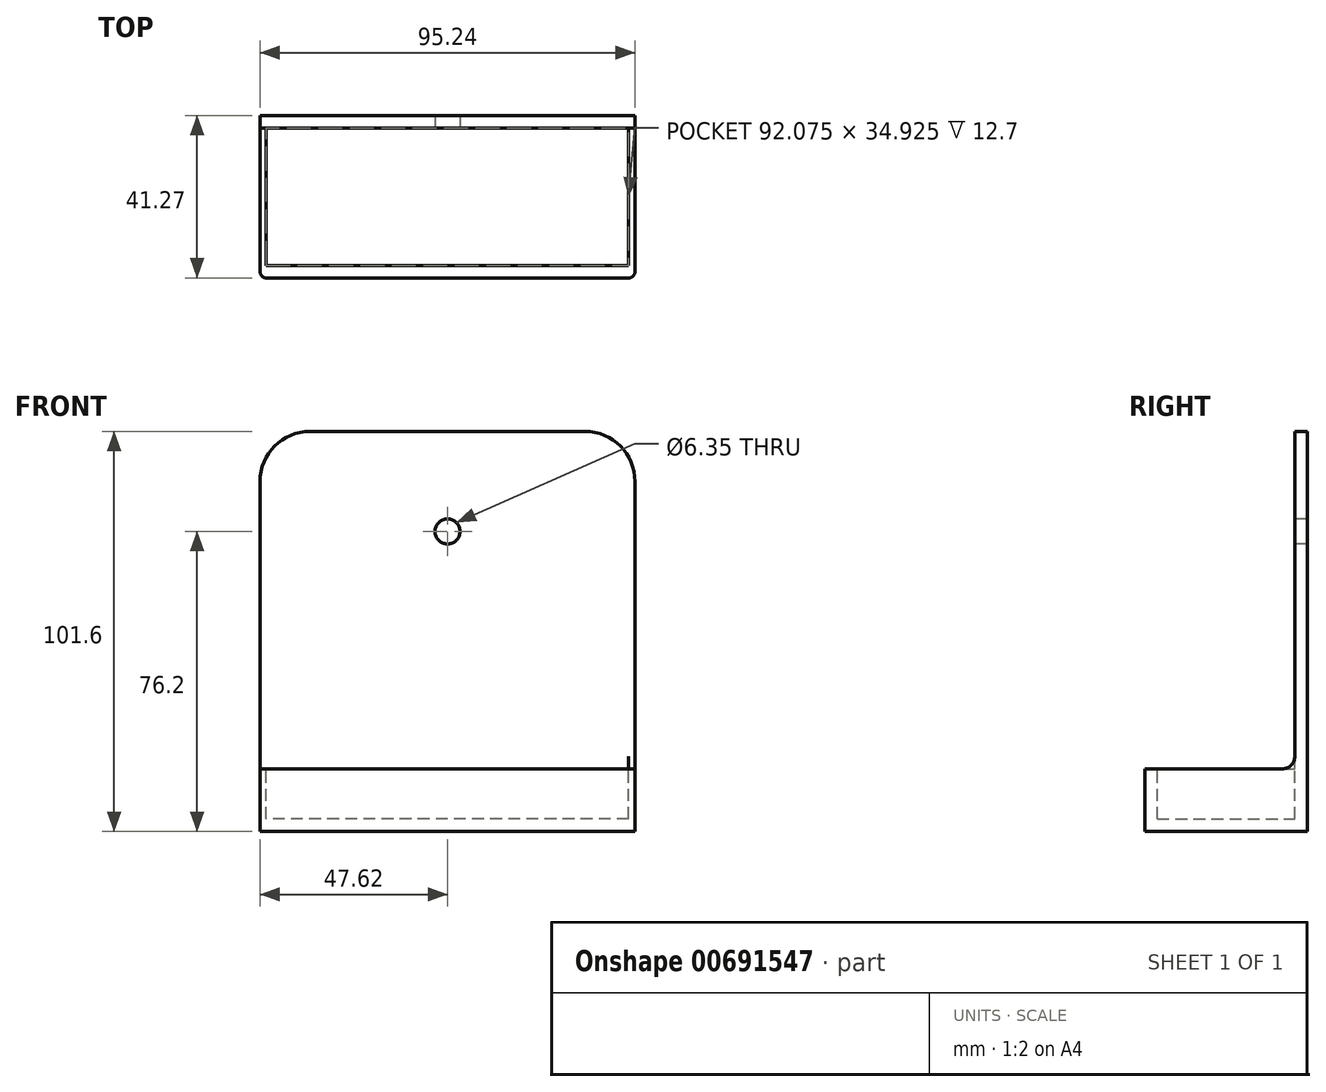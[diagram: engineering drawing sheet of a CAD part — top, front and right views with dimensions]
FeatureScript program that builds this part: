
annotation { "Feature Type Name" : "Feature", "Feature Type Description" : "" }
export const myFeature = defineFeature(function(context is Context, id is Id, definition is map)
    precondition{}
    {
        {
            var Q0;
            Q0=qCreatedBy(makeId("Front.planeOp"),FACE);
            var sketch = newSketch(context, id + "F0", { "sketchPlane" : qUnion([Q0])});
            skLineSegment(sketch, "E0", {"start": v(0, 0) * mm, "end": v(47.63, 0) * mm});
            skLineSegment(sketch, "E1", {"start": v(47.63, 0) * mm, "end": v(47.63, 101.6) * mm});
            skLineSegment(sketch, "E2", {"start": v(47.63, 101.6) * mm, "end": v(0, 101.6) * mm});
            skLineSegment(sketch, "E3", {"start": v(0, 0) * mm, "end": v(0, 39.02) * mm, "construction": true});
            skLineSegment(sketch, "E4.MirrorCS", {"start": v(-47.63, 101.6) * mm, "end": v(0, 101.6) * mm});
            skLineSegment(sketch, "E5.MirrorCS", {"start": v(-47.63, 0) * mm, "end": v(-47.63, 101.6) * mm});
            skLineSegment(sketch, "E6.MirrorCS", {"start": v(0, 0) * mm, "end": v(-47.63, 0) * mm});
            skSolve(sketch);
        }
        {
            var Q0;
            Q0=makeQuery(id+"F0.imprint","IMPRINT",FACE,{"disambiguationData":[TD([[makeQuery(id+"F0.imprint","IMPRINT",EDGE,{"derivedFrom":sQuery(id+"F0.wireOp",EDGE,"E0")}),1.0]])]});
            extrude(context, id + "F1", {"entities" : qUnion([Q0]), "depth" : 3.17 * mm, "offsetDistance" : 25.4 * mm});
        }
        {
            var Q0;
            Q0=qCreatedBy(makeId("Top.planeOp"),FACE);
            var sketch = newSketch(context, id + "F2", { "sketchPlane" : qUnion([Q0])});
            skLineSegment(sketch, "E7", {"start": v(0, 0) * mm, "end": v(-47.63, 0) * mm});
            skLineSegment(sketch, "E8", {"start": v(-47.63, 0) * mm, "end": v(-47.63, -38.1) * mm});
            skLineSegment(sketch, "E9", {"start": v(-47.63, -38.1) * mm, "end": v(0, -38.1) * mm});
            skLineSegment(sketch, "E10", {"start": v(0, 0) * mm, "end": v(0, -19.77) * mm, "construction": true});
            skLineSegment(sketch, "E11.MirrorCS", {"start": v(47.63, 0) * mm, "end": v(47.63, -38.1) * mm});
            skLineSegment(sketch, "E12.MirrorCS", {"start": v(47.63, -38.1) * mm, "end": v(0, -38.1) * mm});
            skLineSegment(sketch, "E13.MirrorCS", {"start": v(0, 0) * mm, "end": v(47.63, 0) * mm});
            skSolve(sketch);
        }
        {
            var Q0;
            Q0=makeQuery(id+"F2.imprint","IMPRINT",FACE,{"disambiguationData":[TD([[makeQuery(id+"F2.imprint","IMPRINT",EDGE,{"derivedFrom":sQuery(id+"F2.wireOp",EDGE,"E7")}),1.0]])]});
            extrude(context, id + "F3", {"entities" : qUnion([Q0]), "operationType" : NewBodyOperationType.ADD, "depth" : 3.17 * mm, "offsetDistance" : 25.4 * mm});
        }
        {
            var Q0;
            Q0=makeQuery(id+"F3.boolean.opBoolean","MERGE",FACE,{"derivedFrom":[makeQuery(id+"F1.opExtrude","SWEPT_FACE",FACE,{"disambiguationData":[OSD([sQuery(id+"F0.wireOp",EDGE,"E1")])]}),makeQuery(id+"F3.opExtrude","SWEPT_FACE",FACE,{"disambiguationData":[OSD([sQuery(id+"F2.wireOp",EDGE,"E11.MirrorCS")])]})]});
            var sketch = newSketch(context, id + "F4", { "sketchPlane" : qUnion([Q0])});
            skLineSegment(sketch, "E14", {"start": v(0, 0) * mm, "end": v(0, 15.88) * mm});
            skLineSegment(sketch, "E15", {"start": v(0, 0) * mm, "end": v(-38.1, 0) * mm});
            skLineSegment(sketch, "E16", {"start": v(-38.1, 0) * mm, "end": v(-38.1, 15.88) * mm});
            skLineSegment(sketch, "E17", {"start": v(-38.1, 15.88) * mm, "end": v(0, 15.88) * mm});
            skSolve(sketch);
        }
        {
            var Q0;
            Q0 = qSketchRegion(id + "F4", true);
            extrude(context, id + "F5", {"entities" : qUnion([Q0]), "operationType" : NewBodyOperationType.ADD, "oppositeDirection" : true, "depth" : 1.59 * mm, "offsetDistance" : 25.4 * mm});
        }
        {
            var Q0;
            Q0=makeQuery(id+"F1.opExtrude","SWEPT_BODY",BODY,{"disambiguationData":[OSD([sQuery(id+"F0.wireOp",EDGE,"E0"),sQuery(id+"F0.wireOp",EDGE,"E1"),sQuery(id+"F0.wireOp",EDGE,"E2"),sQuery(id+"F0.wireOp",EDGE,"E4.MirrorCS"),sQuery(id+"F0.wireOp",EDGE,"E5.MirrorCS"),sQuery(id+"F0.wireOp",EDGE,"E6.MirrorCS")])]});
            var Q1;
            Q1=qCreatedBy(makeId("Right.planeOp"),FACE);
            mirror(context, id + "F6", {"operationType" : NewBodyOperationType.ADD, "entities" : qUnion([Q0]), "mirrorPlane" : qUnion([Q1])});
        }
        {
            var Q0;
            {var subQ0=makeQuery(id+"F5.boolean.opBoolean","MERGE",FACE,{"derivedFrom":[makeQuery(id+"F3.opExtrude","SWEPT_FACE",FACE,{"disambiguationData":[OSD([sQuery(id+"F2.wireOp",EDGE,"E9"),sQuery(id+"F2.wireOp",EDGE,"E12.MirrorCS")])]}),makeQuery(id+"F5.opExtrude","SWEPT_FACE",FACE,{"disambiguationData":[OSD([sQuery(id+"F4.wireOp",EDGE,"E16")])]})]});Q0=makeQuery(id+"F6.boolean.opBoolean","MERGE",FACE,{"derivedFrom":[subQ0,makeQuery(id+"F6.opPattern","COPY",FACE,{"derivedFrom":subQ0,"instanceName":"1"})]});}
            var sketch = newSketch(context, id + "F7", { "sketchPlane" : qUnion([Q0])});
            skLineSegment(sketch, "E18", {"start": v(-47.63, 15.88) * mm, "end": v(47.63, 15.88) * mm});
            skLineSegment(sketch, "E19", {"start": v(47.63, 15.88) * mm, "end": v(47.63, 0) * mm});
            skLineSegment(sketch, "E20", {"start": v(47.63, 0) * mm, "end": v(-47.63, 0) * mm});
            skLineSegment(sketch, "E21", {"start": v(-47.63, 0) * mm, "end": v(-47.63, 15.88) * mm});
            skLineSegment(sketch, "E22", {"start": v(-47.63, 0) * mm, "end": v(47.63, 0) * mm});
            skSolve(sketch);
        }
        {
            var Q0;
            Q0 = qSketchRegion(id + "F7", true);
            extrude(context, id + "F8", {"entities" : qUnion([Q0]), "operationType" : NewBodyOperationType.ADD, "depth" : 3.17 * mm, "offsetDistance" : 25.4 * mm});
        }
        {
            var Q0;
            Q0=makeQuery(id+"F1.opExtrude","SWEPT_EDGE",EDGE,{"disambiguationData":[OSD([sQuery(id+"F0.wireOp",EDGE,"E1"),sQuery(id+"F0.wireOp",EDGE,"E2")])]});
            var Q1;
            Q1=makeQuery(id+"F1.opExtrude","SWEPT_EDGE",EDGE,{"disambiguationData":[OSD([sQuery(id+"F0.wireOp",EDGE,"E4.MirrorCS"),sQuery(id+"F0.wireOp",EDGE,"E5.MirrorCS")])]});
            fillet(context, id + "F9", {"entities" : qUnion([Q0, Q1]), "radius" : 12.7 * mm, "tangentPropagation" : true, "allowEdgeOverflow" : false});
        }
        {
            var Q0;
            Q0=makeQuery(id+"F1.opExtrude","CAP_FACE",FACE,{"disambiguationData":[OSD([sQuery(id+"F0.wireOp",EDGE,"E0"),sQuery(id+"F0.wireOp",EDGE,"E1"),sQuery(id+"F0.wireOp",EDGE,"E2"),sQuery(id+"F0.wireOp",EDGE,"E4.MirrorCS"),sQuery(id+"F0.wireOp",EDGE,"E5.MirrorCS"),sQuery(id+"F0.wireOp",EDGE,"E6.MirrorCS")])],"isStart":false});
            var sketch = newSketch(context, id + "F10", { "sketchPlane" : qUnion([Q0])});
            skLineSegment(sketch, "E23", {"start": v(0, 101.6) * mm, "end": v(0, 76.2) * mm, "construction": true});
            skSolve(sketch);
        }
        {
            var Q0;
            Q0=sQuery(id+"F10.wireOp",VERTEX,"E23.end");
            var Q1;
            Q1=makeQuery(id+"F1.opExtrude","SWEPT_BODY",BODY,{"disambiguationData":[OSD([sQuery(id+"F0.wireOp",EDGE,"E0"),sQuery(id+"F0.wireOp",EDGE,"E1"),sQuery(id+"F0.wireOp",EDGE,"E2"),sQuery(id+"F0.wireOp",EDGE,"E4.MirrorCS"),sQuery(id+"F0.wireOp",EDGE,"E5.MirrorCS"),sQuery(id+"F0.wireOp",EDGE,"E6.MirrorCS")])]});
            hole(context, id + "F11", {"style" : HoleStyle.SIMPLE, "endStyle" : HoleEndStyle.THROUGH, "holeDiameter" : 6.35 * mm, "majorDiameter" : 6.35 * mm, "isTappedThrough" : true, "tappedDepth" : 12.7 * mm, "tapClearance" : 3, "locations" : qUnion([Q0]), "scope" : qUnion([Q1])});
        }
        {
            var Q0;
            Q0=makeQuery(id+"F6.opPattern","COPY",EDGE,{"derivedFrom":makeQuery(id+"F5.boolean.opBoolean","INTERSECT",EDGE,{"derivedFrom":[makeQuery(id+"F1.opExtrude","CAP_FACE",FACE,{"disambiguationData":[OSD([sQuery(id+"F0.wireOp",EDGE,"E0"),sQuery(id+"F0.wireOp",EDGE,"E1"),sQuery(id+"F0.wireOp",EDGE,"E2"),sQuery(id+"F0.wireOp",EDGE,"E4.MirrorCS"),sQuery(id+"F0.wireOp",EDGE,"E5.MirrorCS"),sQuery(id+"F0.wireOp",EDGE,"E6.MirrorCS")])],"isStart":false}),makeQuery(id+"F5.opExtrude","SWEPT_FACE",FACE,{"disambiguationData":[OSD([sQuery(id+"F4.wireOp",EDGE,"E17")])]})]}),"instanceName":"1"});
            var Q1;
            Q1=makeQuery(id+"F5.boolean.opBoolean","INTERSECT",EDGE,{"derivedFrom":[makeQuery(id+"F1.opExtrude","CAP_FACE",FACE,{"disambiguationData":[OSD([sQuery(id+"F0.wireOp",EDGE,"E0"),sQuery(id+"F0.wireOp",EDGE,"E1"),sQuery(id+"F0.wireOp",EDGE,"E2"),sQuery(id+"F0.wireOp",EDGE,"E4.MirrorCS"),sQuery(id+"F0.wireOp",EDGE,"E5.MirrorCS"),sQuery(id+"F0.wireOp",EDGE,"E6.MirrorCS")])],"isStart":false}),makeQuery(id+"F5.opExtrude","SWEPT_FACE",FACE,{"disambiguationData":[OSD([sQuery(id+"F4.wireOp",EDGE,"E17")])]})]});
            fillet(context, id + "F12", {"entities" : qUnion([Q0, Q1]), "radius" : 3.17 * mm, "tangentPropagation" : true, "allowEdgeOverflow" : false});
        }
        {
            var Q0;
            Q0=makeQuery(id+"F8.opExtrude","CAP_EDGE",EDGE,{"disambiguationData":[OSD([sQuery(id+"F7.wireOp",EDGE,"E21")])],"isStart":false});
            var Q1;
            Q1=makeQuery(id+"F8.opExtrude","CAP_EDGE",EDGE,{"disambiguationData":[OSD([sQuery(id+"F7.wireOp",EDGE,"E19")])],"isStart":false});
            fillet(context, id + "F13", {"entities" : qUnion([Q0, Q1]), "radius" : 1.59 * mm, "tangentPropagation" : true, "allowEdgeOverflow" : false});
        }
    });
